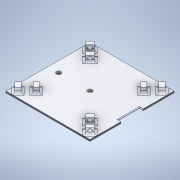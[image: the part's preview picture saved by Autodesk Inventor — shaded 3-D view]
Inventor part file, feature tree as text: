
AUTODESK INVENTOR PART (.ipt)
format: ipt  version: 2022 (Build 260153000, 153)  size: 320,512 bytes
history: native  units: in
note: dims shown in document units (in); Inventor stores cm internally (conversion verified against a paired STEP export)
features: sketch x7, extrude x4, hole x3, fillet x2, chamfer x1, pattern_circular x1
ambient origin geometry x8: Origin, YZ Plane, XZ Plane, XY Plane, X Axis, Y Axis, Z Axis, Center Point
bodies: Solid1 (feature_tree)
feature tree (18):
  extrude  "Extrusion1"  Depth=2.9528in
  hole  "Hole2"  [1 undecoded]
  chamfer  "Chamfer1"  Distance=0.0787in Angle=45.0deg
  hole  "Hole5"  [1 undecoded]
  extrude  "Extrusion5"  Depth=0.2165in
  fillet  "Fillet3"  Radius=0.1575in
  hole  "Hole7"  [1 undecoded]
  pattern_circular  "Circular Pattern6"  [2 undecoded]
  extrude  "Extrusion6"  Depth=0.0197in
  extrude  "Extrusion7"  Depth=0.0197in
  fillet  "Fillet4"  Radius=0.1082in
  sketch  "Sketch1"  dims[d0=2.9528in d1=2.9528in]
  sketch  "Sketch4"  dims[d2=0.1378in d3=0.0in]
  sketch  "Sketch9"  dims[d15=0.1575in d16=0.2362in d17=1.0039in d18=0.0591in d19=90.0deg d20=0.315in d21=0.8108in d22=1.4764in]
  sketch  "Sketch11"  dims[d23=1.4764in d24=0.0787in d25=0.0787in d26=45.0deg]
  sketch  "Sketch13"  dims[d82=0.1575in d83=0.2362in d84=0.1575in d85=0.0787in d86=90.0deg d87=0.315in d88=0.8108in d89=1.1024in]
  sketch  "Sketch14"  dims[d90=1.4764in d97=0.2165in d98=0.1575in]
  sketch  "Sketch15"  dims[d99=0.9276in d100=0.1969in d101=0.0in d102=0.1575in d103=0.2953in d105=0.2165in d106=0.1082in d107=0.0787in d117=0.1181in d118=0.2362in d119=0.1575in d120=0.0787in d121=90.0deg d122=0.315in d123=0.8108in d124=0.1083in d125=0.0787in d129=1.5748in d130=360.0deg d132=0.8661in d133=0.9843in d134=0.9843in d135=0.0787in d136=0.0787in d137=0.0984in d138=0.7874in d140=0.8268in d141=0.7874in d143=0.4921in d146=0.0787in d147=0.0in d148=0.1181in d149=0.7874in d150=0.0984in d151=0.0in d152=0.0in d153=0.0197in d131=0.0197in]
note: 5 required parameter values undecoded (feature->parameter linkage not recoverable at this tier; creation-order binding heuristic only, values carry confidence <= 0.55)
